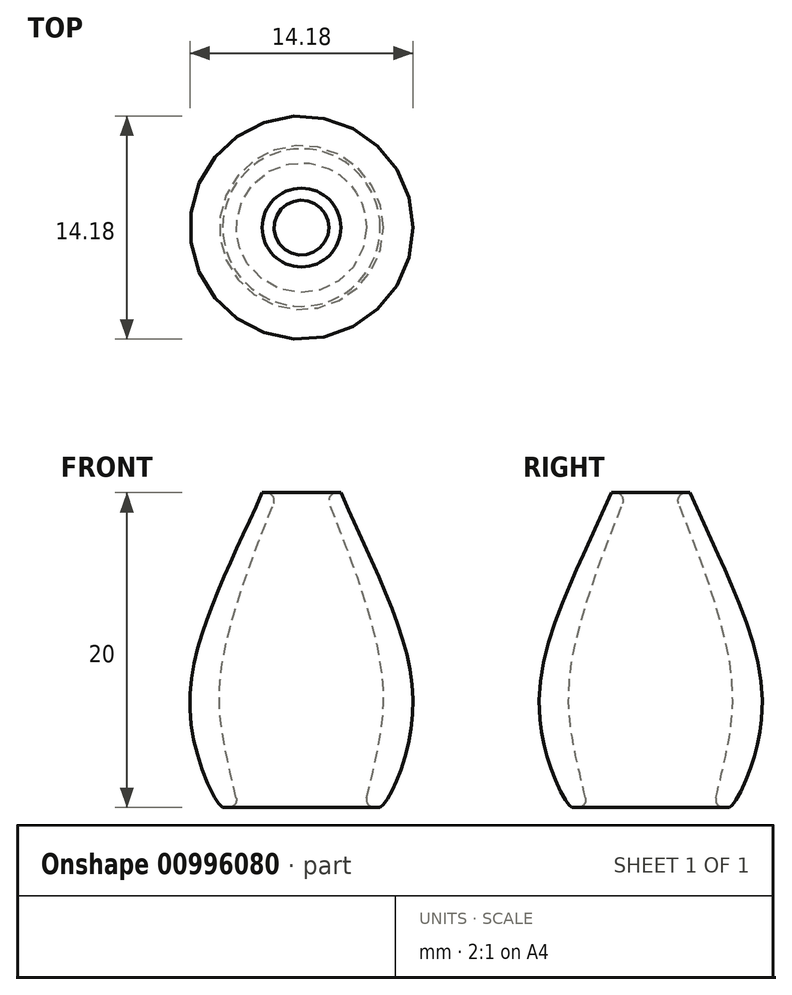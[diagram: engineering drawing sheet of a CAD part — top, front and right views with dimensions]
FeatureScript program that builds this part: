
annotation { "Feature Type Name" : "Feature", "Feature Type Description" : "" }
export const myFeature = defineFeature(function(context is Context, id is Id, definition is map)
    precondition{}
    {
        {
            var Q0;
            Q0=qCreatedBy(makeId("Front.planeOp"),FACE);
            var sketch = newSketch(context, id + "F0", { "sketchPlane" : qUnion([Q0])});
            skFitSpline(sketch, "E0.MirrorCS", {"points": [v(-5, 0) * mm, v(-7.08, 6.08) * mm, v(-2.5, 20) * mm], "startDerivative": vector(-4.28, 2.62) * mm, "endDerivative": vector(11.25, 25.81) * mm});
            skLineSegment(sketch, "E1", {"start": v(-4, 0) * mm, "end": v(-5, 0) * mm});
            skLineSegment(sketch, "E2", {"start": v(-2.5, 20) * mm, "end": v(-1.5, 20) * mm});
            skFitSpline(sketch, "E3", {"points": [v(-4, 0) * mm, v(-5.15, 8.17) * mm, v(-1.5, 20) * mm], "startDerivative": vector(-5.19, 22.55) * mm, "endDerivative": vector(9.27, 23.25) * mm});
            skLineSegment(sketch, "E4", {"start": v(0, 0) * mm, "end": v(-4, 0) * mm});
            skLineSegment(sketch, "E5", {"start": v(-1.5, 20) * mm, "end": v(0, 20) * mm});
            skLineSegment(sketch, "E6", {"start": v(0, 20) * mm, "end": v(0, 0) * mm});
            skSolve(sketch);
        }
        {
            var Q0;
            Q0=makeQuery(id+"F0.imprint","IMPRINT",FACE,{"disambiguationData":[TD([[makeQuery(id+"F0.imprint","IMPRINT",EDGE,{"derivedFrom":sQuery(id+"F0.wireOp",EDGE,"E0.MirrorCS")}),-1.0]])]});
            var Q1;
            Q1=sQuery(id+"F0.wireOp",EDGE,"E6");
            revolve(context, id + "F1", {"surfaceOperationType" : NewSurfaceOperationType.NEW, "entities" : qUnion([Q0]), "axis" : qUnion([Q1]), "revolveType" : RevolveType.FULL});
        }
        {
            var Q0;
            Q0=makeQuery(id+"F1.opRevolve","SWEPT_EDGE",EDGE,{"disambiguationData":[OSD([sQuery(id+"F0.wireOp",EDGE,"E2"),sQuery(id+"F0.wireOp",EDGE,"E3"),sQuery(id+"F0.wireOp",EDGE,"E5")])]});
            fillet(context, id + "F2", {"entities" : qUnion([Q0]), "radius" : .5 * mm, "tangentPropagation" : true, "allowEdgeOverflow" : false});
        }
        {
            var Q0;
            Q0=makeQuery(id+"F1.opRevolve","SWEPT_EDGE",EDGE,{"disambiguationData":[OSD([sQuery(id+"F0.wireOp",EDGE,"E1"),sQuery(id+"F0.wireOp",EDGE,"E3"),sQuery(id+"F0.wireOp",EDGE,"E4")])]});
            fillet(context, id + "F3", {"entities" : qUnion([Q0]), "radius" : .5 * mm, "tangentPropagation" : true, "allowEdgeOverflow" : false});
        }
    });
